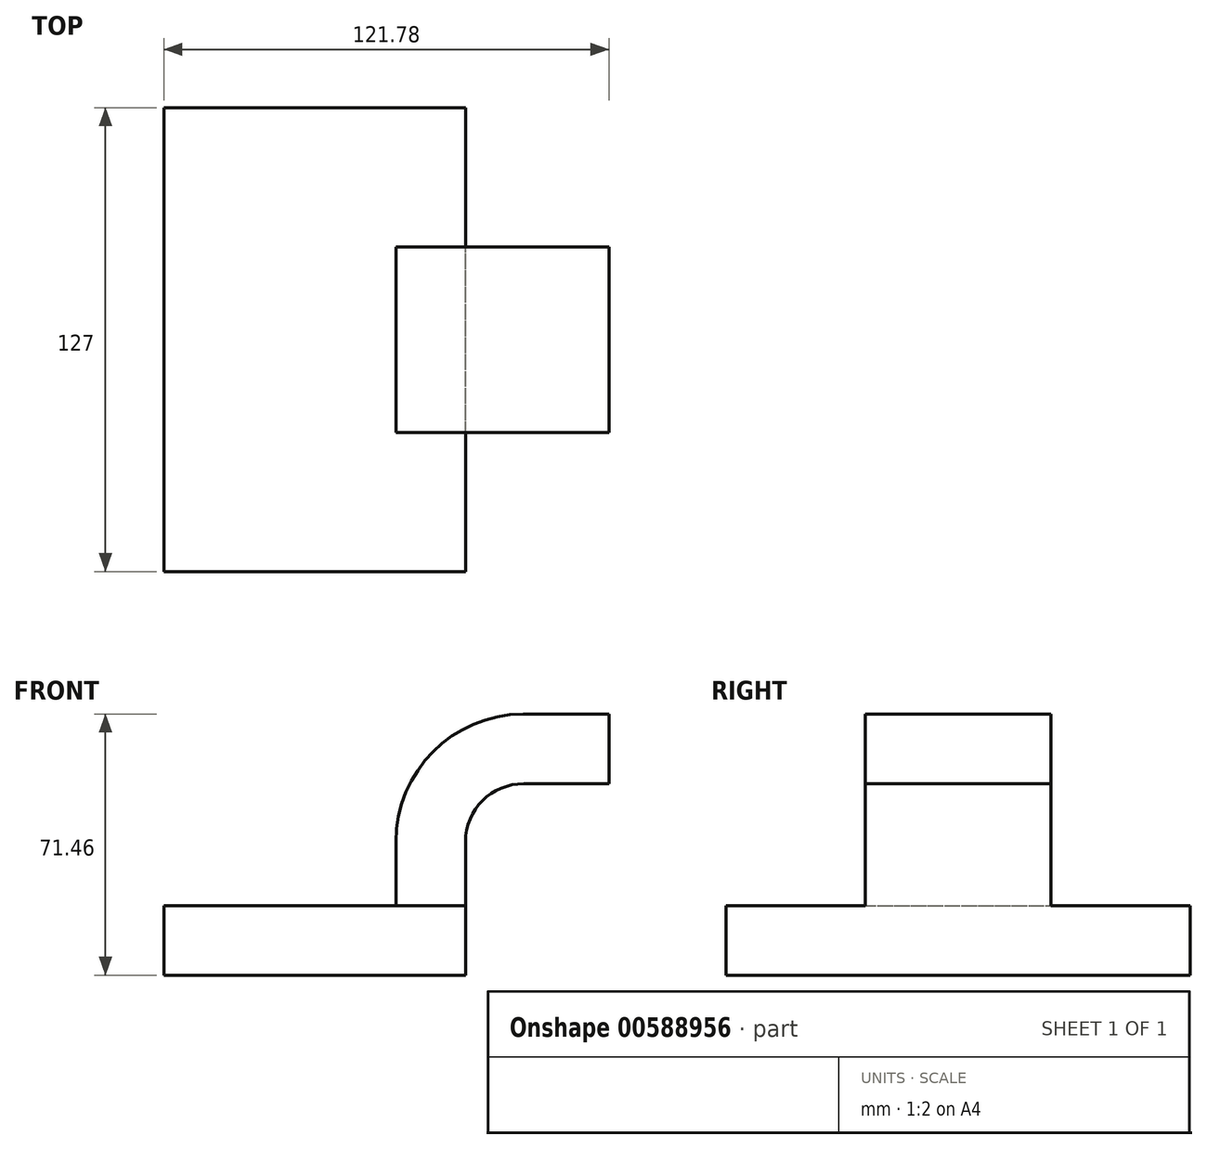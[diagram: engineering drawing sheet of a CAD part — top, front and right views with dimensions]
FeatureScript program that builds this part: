
annotation { "Feature Type Name" : "Feature", "Feature Type Description" : "" }
export const myFeature = defineFeature(function(context is Context, id is Id, definition is map)
    precondition{}
    {
        {
            var Q0;
            Q0=qCreatedBy(makeId("Front.planeOp"),FACE);
            var sketch = newSketch(context, id + "F0", { "sketchPlane" : qUnion([Q0])});
            skLineSegment(sketch, "E0.bottom", {"start": v(-41.28, -9.53) * mm, "end": v(41.28, -9.53) * mm});
            skLineSegment(sketch, "E0.top", {"start": v(-41.28, 9.53) * mm, "end": v(41.28, 9.53) * mm});
            skLineSegment(sketch, "E0.left", {"start": v(-41.28, -9.53) * mm, "end": v(-41.28, 9.53) * mm});
            skLineSegment(sketch, "E0.right", {"start": v(41.28, -9.53) * mm, "end": v(41.28, 9.53) * mm});
            skPoint(sketch, "E0.middle", {"position": v(0, 0) * mm});
            skLineSegment(sketch, "E1.bottom", {"start": v(111.12, 38.1) * mm, "end": v(60.32, 38.1) * mm});
            skLineSegment(sketch, "E1.top", {"start": v(111.12, 66.68) * mm, "end": v(60.32, 66.68) * mm});
            skLineSegment(sketch, "E1.left", {"start": v(111.12, 38.1) * mm, "end": v(111.12, 66.68) * mm});
            skLineSegment(sketch, "E1.right", {"start": v(60.32, 38.1) * mm, "end": v(60.32, 66.67) * mm});
            skPoint(sketch, "E1.middle", {"position": v(85.72, 52.39) * mm});
            skLineSegment(sketch, "E2", {"start": v(41.28, 9.53) * mm, "end": v(41.28, 27) * mm});
            skArc(sketch, "E3", {"start": v(41.28, 27) * mm, "mid": v(45.92, 38.23) * mm, "end": v(57.15, 42.88) * mm});
            skLineSegment(sketch, "E4", {"start": v(57.15, 42.88) * mm, "end": v(80.5, 42.88) * mm});
            skLineSegment(sketch, "E5.0", {"start": v(57.15, 61.93) * mm, "end": v(80.5, 61.93) * mm});
            skArc(sketch, "E5.1", {"start": v(22.23, 27) * mm, "mid": v(32.45, 51.7) * mm, "end": v(57.15, 61.93) * mm});
            skLineSegment(sketch, "E5.2", {"start": v(22.23, 9.53) * mm, "end": v(22.23, 27) * mm});
            skLineSegment(sketch, "E6", {"start": v(80.5, 61.93) * mm, "end": v(80.5, 42.88) * mm});
            skFitSpline(sketch, "E7", {"points": [v(-41.28, 9.53) * mm, v(57.15, 61.93) * mm], "startDerivative": vector(1.52, 57.86) * mm, "endDerivative": vector(131.99, 0.2) * mm});
            skSolve(sketch);
        }
        {
            var Q0;
            Q0=makeQuery(id+"F0.imprint","IMPRINT",FACE,{"disambiguationData":[TD([[makeQuery(id+"F0.imprint","IMPRINT",EDGE,{"derivedFrom":sQuery(id+"F0.wireOp",EDGE,"E0.bottom")}),1.0]])]});
            extrude(context, id + "F1", {"entities" : qUnion([Q0]), "endBound" : BoundingType.SYMMETRIC, "depth" : 127 * mm, "offsetDistance" : 25.4 * mm});
        }
        {
            var Q0;
            {var subQ0=sQuery(id+"F0.wireOp",EDGE,"E2");Q0=makeQuery(id+"F0.imprint","IMPRINT",FACE,{"disambiguationData":[TD([[makeQuery(id+"F0.imprint","IMPRINT",EDGE,{"derivedFrom":subQ0}),1.0]])]});}
            var Q1;
            {var subQ5=sQuery(id+"F0.wireOp",EDGE,"E6");Q1=makeQuery(id+"F0.imprint","IMPRINT",FACE,{"disambiguationData":[TD([[makeQuery(id+"F0.imprint","IMPRINT",EDGE,{"derivedFrom":subQ5}),-1.0]])]});}
            extrude(context, id + "F2", {"entities" : qUnion([Q0, Q1]), "operationType" : NewBodyOperationType.ADD, "endBound" : BoundingType.SYMMETRIC, "depth" : 50.8 * mm, "offsetDistance" : 25.4 * mm});
        }
        {
            var Q0;
            {var subQ4=sQuery(id+"F0.wireOp",EDGE,"E5.1");Q0=makeQuery(id+"F0.imprint","IMPRINT",FACE,{"disambiguationData":[TD([[makeQuery(id+"F0.imprint","IMPRINT",EDGE,{"derivedFrom":subQ4}),1.0]])]});}
            extrude(context, id + "F3", {"entities" : qUnion([Q0]), "operationType" : NewBodyOperationType.ADD, "endBound" : BoundingType.SYMMETRIC, "depth" : 15.88 * mm, "offsetDistance" : 25.4 * mm});
        }
    });
